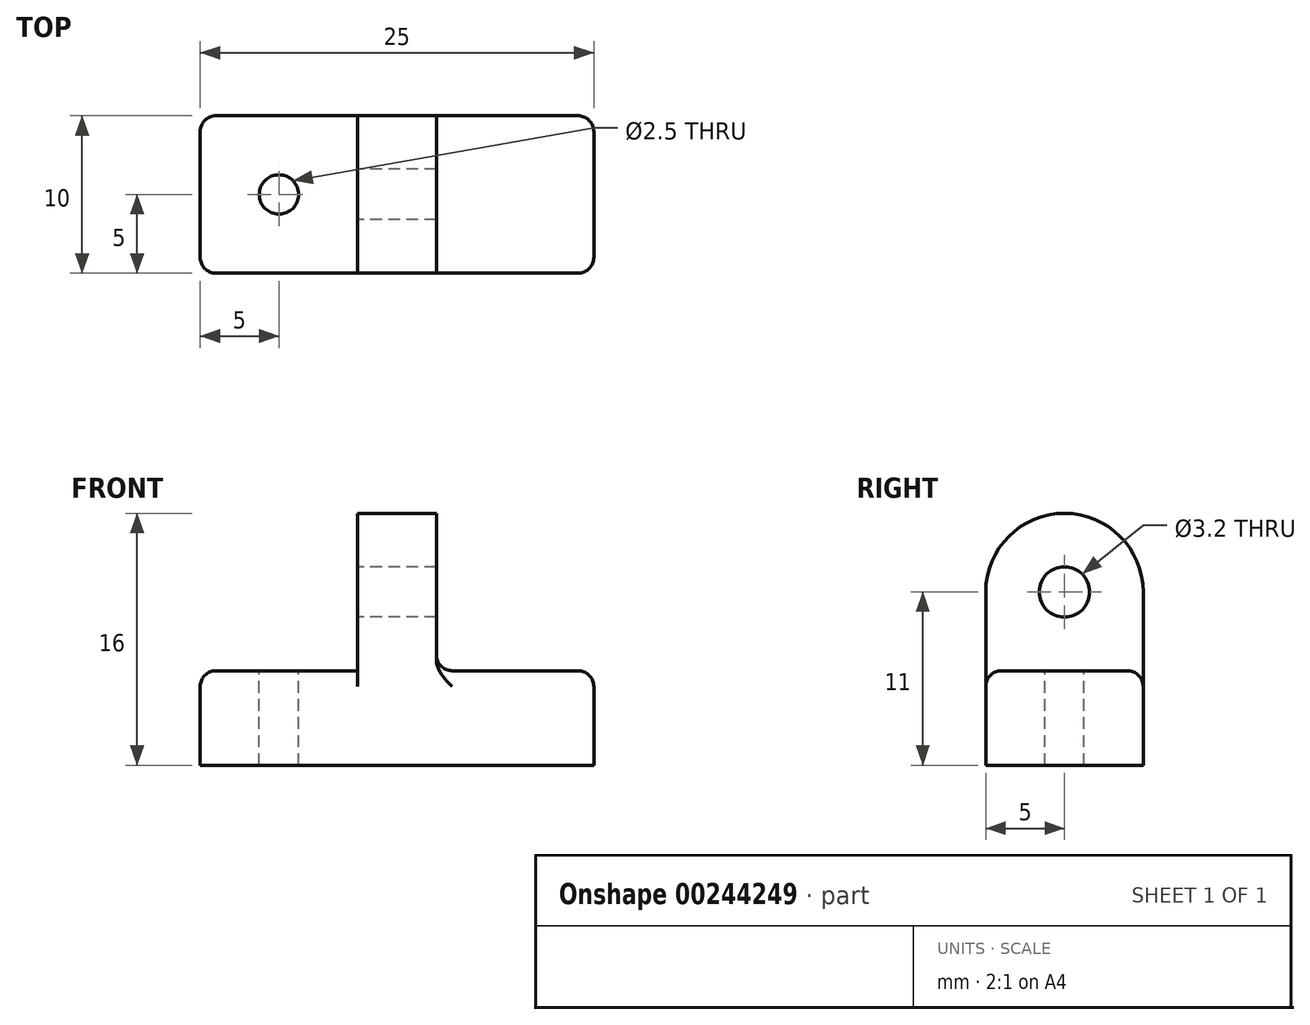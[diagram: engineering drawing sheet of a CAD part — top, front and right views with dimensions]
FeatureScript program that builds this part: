
annotation { "Feature Type Name" : "Feature", "Feature Type Description" : "" }
export const myFeature = defineFeature(function(context is Context, id is Id, definition is map)
    precondition{}
    {
        {
            var Q0;
            Q0=qCreatedBy(makeId("Top.planeOp"),FACE);
            var sketch = newSketch(context, id + "F0", { "sketchPlane" : qUnion([Q0])});
            skLineSegment(sketch, "E0.bottom", {"start": v(12.5, 5) * mm, "end": v(-12.5, 5) * mm});
            skLineSegment(sketch, "E0.top", {"start": v(12.5, -5) * mm, "end": v(-12.5, -5) * mm});
            skLineSegment(sketch, "E0.left", {"start": v(12.5, 5) * mm, "end": v(12.5, -5) * mm});
            skLineSegment(sketch, "E0.right", {"start": v(-12.5, 5) * mm, "end": v(-12.5, -5) * mm});
            skPoint(sketch, "E0.middle", {"position": v(0, 0) * mm});
            skSolve(sketch);
        }
        {
            var Q0;
            Q0=qSketchRegion(id+"F0",true);
            extrude(context, id + "F1", {"entities" : qUnion([Q0]), "depth" : 6 * mm});
        }
        {
            var Q0;
            Q0=makeQuery(id+"F1.opExtrude","CAP_FACE",FACE,{"disambiguationData":[OSD([sQuery(id+"F0.wireOp",EDGE,"E0.bottom"),sQuery(id+"F0.wireOp",EDGE,"E0.top"),sQuery(id+"F0.wireOp",EDGE,"E0.left"),sQuery(id+"F0.wireOp",EDGE,"E0.right")])],"isStart":false});
            var sketch = newSketch(context, id + "F2", { "sketchPlane" : qUnion([Q0])});
            skLineSegment(sketch, "E1.bottom", {"start": v(2.5, 5) * mm, "end": v(-2.5, 5) * mm});
            skLineSegment(sketch, "E1.top", {"start": v(2.5, -5) * mm, "end": v(-2.5, -5) * mm});
            skLineSegment(sketch, "E1.left", {"start": v(2.5, 5) * mm, "end": v(2.5, -5) * mm});
            skLineSegment(sketch, "E1.right", {"start": v(-2.5, 5) * mm, "end": v(-2.5, -5) * mm});
            skPoint(sketch, "E1.middle", {"position": v(0, 0) * mm});
            skSolve(sketch);
        }
        {
            var Q0;
            Q0=qSketchRegion(id+"F2",true);
            extrude(context, id + "F3", {"entities" : qUnion([Q0]), "operationType" : NewBodyOperationType.ADD, "depth" : 10 * mm});
        }
        {
            var Q0;
            {var subQ0=sQuery(id+"F0.wireOp",EDGE,"E0.right");var subQ1=sQuery(id+"F0.wireOp",EDGE,"E0.top");var subQ2=sQuery(id+"F0.wireOp",EDGE,"E0.bottom");Q0=makeQuery(id+"F3.boolean.opBoolean","SPLIT",FACE,{"disambiguationData":[TD([makeQuery(id+"F1.opExtrude","SWEPT_FACE",FACE,{"disambiguationData":[OSD([subQ0])]})])],"derivedFrom":makeQuery(id+"F1.opExtrude","CAP_FACE",FACE,{"disambiguationData":[OSD([subQ2,subQ1,sQuery(id+"F0.wireOp",EDGE,"E0.left"),subQ0])],"isStart":false})});}
            var sketch = newSketch(context, id + "F4", { "sketchPlane" : qUnion([Q0])});
            skCircle(sketch, "E2", {"center": v(-7.5, 0) * mm, "radius": 1.25 * mm});
            skLineSegment(sketch, "E3", {"start": v(-12.5, 5) * mm, "end": v(-2.5, -5) * mm, "construction": true});
            skSolve(sketch);
        }
        {
            var Q0;
            Q0=qSketchRegion(id+"F4",true);
            extrude(context, id + "F5", {"entities" : qUnion([Q0]), "operationType" : NewBodyOperationType.REMOVE, "endBound" : BoundingType.THROUGH_ALL, "oppositeDirection" : true, "depth" : 25 * mm});
        }
        {
            var Q0;
            Q0=makeQuery(id+"F3.opExtrude","CAP_EDGE",EDGE,{"disambiguationData":[OSD([sQuery(id+"F2.wireOp",EDGE,"E1.top")])],"isStart":false});
            var Q1;
            Q1=makeQuery(id+"F3.opExtrude","CAP_EDGE",EDGE,{"disambiguationData":[OSD([sQuery(id+"F2.wireOp",EDGE,"E1.bottom")])],"isStart":false});
            fillet(context, id + "F6", {"entities" : qUnion([Q0, Q1]), "radius" : 5 * mm, "tangentPropagation" : true, "allowEdgeOverflow" : false});
        }
        {
            var Q0;
            Q0=makeQuery(id+"F3.opExtrude","SWEPT_FACE",FACE,{"disambiguationData":[OSD([sQuery(id+"F2.wireOp",EDGE,"E1.right")])]});
            var sketch = newSketch(context, id + "F7", { "sketchPlane" : qUnion([Q0])});
            skLineSegment(sketch, "E4", {"start": v(5, 11) * mm, "end": v(-5, 11) * mm, "construction": true});
            skCircle(sketch, "E5", {"center": v(0, 11) * mm, "radius": 1.6 * mm});
            skSolve(sketch);
        }
        {
            var Q0;
            Q0=qSketchRegion(id+"F7",true);
            extrude(context, id + "F8", {"entities" : qUnion([Q0]), "operationType" : NewBodyOperationType.REMOVE, "endBound" : BoundingType.THROUGH_ALL, "oppositeDirection" : true, "depth" : 25 * mm});
        }
        {
            var Q0;
            {var subQ0=sQuery(id+"F0.wireOp",EDGE,"E0.left");var subQ1=sQuery(id+"F0.wireOp",EDGE,"E0.top");Q0=makeQuery(id+"F3.boolean.opBoolean","SPLIT",EDGE,{"disambiguationData":[TD([makeQuery(id+"F1.opExtrude","SWEPT_FACE",FACE,{"disambiguationData":[OSD([subQ0])]})])],"derivedFrom":makeQuery(id+"F1.opExtrude","CAP_EDGE",EDGE,{"disambiguationData":[OSD([subQ1])],"isStart":false})});}
            var Q1;
            Q1=makeQuery(id+"F1.opExtrude","CAP_EDGE",EDGE,{"disambiguationData":[OSD([sQuery(id+"F0.wireOp",EDGE,"E0.left")])],"isStart":false});
            var Q2;
            {var subQ0=sQuery(id+"F0.wireOp",EDGE,"E0.left");var subQ1=sQuery(id+"F0.wireOp",EDGE,"E0.bottom");Q2=makeQuery(id+"F3.boolean.opBoolean","SPLIT",EDGE,{"disambiguationData":[TD([makeQuery(id+"F1.opExtrude","SWEPT_FACE",FACE,{"disambiguationData":[OSD([subQ0])]})])],"derivedFrom":makeQuery(id+"F1.opExtrude","CAP_EDGE",EDGE,{"disambiguationData":[OSD([subQ1])],"isStart":false})});}
            var Q3;
            Q3=makeQuery(id+"F1.opExtrude","SWEPT_EDGE",EDGE,{"disambiguationData":[OSD([sQuery(id+"F0.wireOp",EDGE,"E0.top"),sQuery(id+"F0.wireOp",EDGE,"E0.left")])]});
            var Q4;
            Q4=makeQuery(id+"F1.opExtrude","SWEPT_EDGE",EDGE,{"disambiguationData":[OSD([sQuery(id+"F0.wireOp",EDGE,"E0.bottom"),sQuery(id+"F0.wireOp",EDGE,"E0.left")])]});
            var Q5;
            Q5=makeQuery(id+"F1.opExtrude","SWEPT_EDGE",EDGE,{"disambiguationData":[OSD([sQuery(id+"F0.wireOp",EDGE,"E0.top"),sQuery(id+"F0.wireOp",EDGE,"E0.right")])]});
            var Q6;
            Q6=makeQuery(id+"F1.opExtrude","SWEPT_EDGE",EDGE,{"disambiguationData":[OSD([sQuery(id+"F0.wireOp",EDGE,"E0.bottom"),sQuery(id+"F0.wireOp",EDGE,"E0.right")])]});
            var Q7;
            Q7=makeQuery(id+"F1.opExtrude","CAP_EDGE",EDGE,{"disambiguationData":[OSD([sQuery(id+"F0.wireOp",EDGE,"E0.right")])],"isStart":false});
            var Q8;
            {var subQ0=sQuery(id+"F0.wireOp",EDGE,"E0.right");var subQ1=sQuery(id+"F0.wireOp",EDGE,"E0.top");Q8=makeQuery(id+"F3.boolean.opBoolean","SPLIT",EDGE,{"disambiguationData":[TD([makeQuery(id+"F1.opExtrude","SWEPT_FACE",FACE,{"disambiguationData":[OSD([subQ0])]})])],"derivedFrom":makeQuery(id+"F1.opExtrude","CAP_EDGE",EDGE,{"disambiguationData":[OSD([subQ1])],"isStart":false})});}
            var Q9;
            {var subQ0=sQuery(id+"F0.wireOp",EDGE,"E0.right");var subQ1=sQuery(id+"F0.wireOp",EDGE,"E0.bottom");Q9=makeQuery(id+"F3.boolean.opBoolean","SPLIT",EDGE,{"disambiguationData":[TD([makeQuery(id+"F1.opExtrude","SWEPT_FACE",FACE,{"disambiguationData":[OSD([subQ0])]})])],"derivedFrom":makeQuery(id+"F1.opExtrude","CAP_EDGE",EDGE,{"disambiguationData":[OSD([subQ1])],"isStart":false})});}
            fillet(context, id + "F9", {"entities" : qUnion([Q0, Q1, Q2, Q3, Q4, Q5, Q6, Q7, Q8, Q9]), "radius" : 1 * mm, "tangentPropagation" : true, "allowEdgeOverflow" : false});
        }
        {
            var Q0;
            Q0=makeQuery(id+"F3.opExtrude","CAP_EDGE",EDGE,{"disambiguationData":[OSD([sQuery(id+"F2.wireOp",EDGE,"E1.left")])],"isStart":true});
            var Q1;
            Q1=makeQuery(id+"F3.opExtrude","CAP_EDGE",EDGE,{"disambiguationData":[OSD([sQuery(id+"F2.wireOp",EDGE,"E1.right")])],"isStart":true});
            fillet(context, id + "F10", {"entities" : qUnion([Q0, Q1]), "radius" : 1 * mm, "tangentPropagation" : true, "allowEdgeOverflow" : false});
        }
    });
